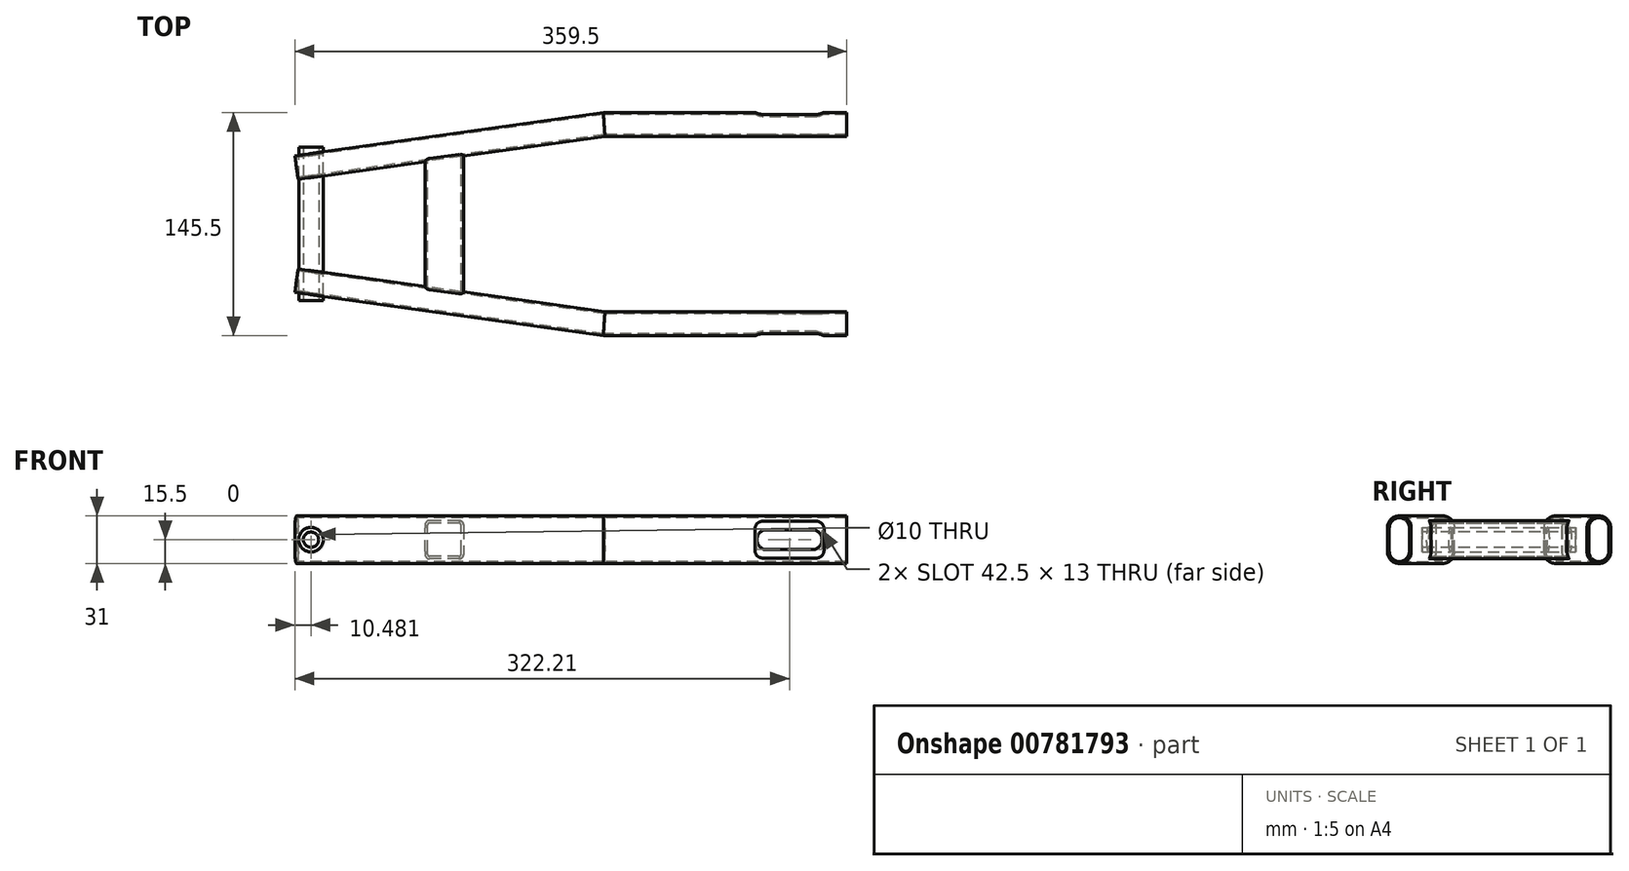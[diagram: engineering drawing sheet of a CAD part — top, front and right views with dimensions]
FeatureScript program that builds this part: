
annotation { "Feature Type Name" : "Feature", "Feature Type Description" : "" }
export const myFeature = defineFeature(function(context is Context, id is Id, definition is map)
    precondition{}
    {
        {
            var Q0;
            Q0=qCreatedBy(makeId("Top.planeOp"),FACE);
            var sketch = newSketch(context, id + "F0", { "sketchPlane" : qUnion([Q0])});
            skLineSegment(sketch, "E0", {"start": v(0, 65) * mm, "end": v(-158.03, 65) * mm});
            skLineSegment(sketch, "E1", {"start": v(-158.03, 65) * mm, "end": v(-358.42, 36.84) * mm});
            skSolve(sketch);
        }
        {
            var Q0;
            Q0=qCreatedBy(makeId("Right.planeOp"),FACE);
            var sketch = newSketch(context, id + "F1", { "sketchPlane" : qUnion([Q0])});
            skLineSegment(sketch, "E2.left", {"start": v(72.75, -7.75) * mm, "end": v(72.75, 7.75) * mm});
            skLineSegment(sketch, "E2.right", {"start": v(57.25, -7.75) * mm, "end": v(57.25, 7.75) * mm});
            skArc(sketch, "E3", {"start": v(57.25, 7.75) * mm, "mid": v(65, 15.5) * mm, "end": v(72.75, 7.75) * mm});
            skArc(sketch, "E4", {"start": v(72.75, -7.75) * mm, "mid": v(65, -15.5) * mm, "end": v(57.25, -7.75) * mm});
            skLineSegment(sketch, "E5.0", {"start": v(58.45, -7.75) * mm, "end": v(58.45, 7.75) * mm});
            skLineSegment(sketch, "E6.0", {"start": v(71.55, -7.75) * mm, "end": v(71.55, 7.75) * mm});
            skArc(sketch, "E7.0", {"start": v(71.55, -7.75) * mm, "mid": v(65, -14.3) * mm, "end": v(58.45, -7.75) * mm});
            skArc(sketch, "E8.0", {"start": v(58.45, 7.75) * mm, "mid": v(65, 14.3) * mm, "end": v(71.55, 7.75) * mm});
            skSolve(sketch);
        }
        {
            var Q0;
            Q0 = qSketchRegion(id + "F1", true);
            var Q1;
            Q1 = qConstructionFilter(qBodyType(qCreatedBy(id + "F0" ,EDGE), BodyType.WIRE), ConstructionObject.NO);
            sweep(context, id + "F2", {"profiles" : qUnion([Q0]), "path" : qUnion([Q1])});
        }
        {
            var Q0;
            Q0=makeQuery(id+"F2.opSweep","SWEPT_FACE",FACE,{"disambiguationData":[OSD([sQuery(id+"F0.wireOp",EDGE,"E0"),sQuery(id+"F1.wireOp",EDGE,"E2.right")])]});
            var sketch = newSketch(context, id + "F3", { "sketchPlane" : qUnion([Q0])});
            skLineSegment(sketch, "E9.bottom", {"start": v(-22.54, -6.5) * mm, "end": v(-52.04, -6.5) * mm});
            skLineSegment(sketch, "E9.top", {"start": v(-22.54, 6.5) * mm, "end": v(-52.04, 6.5) * mm});
            skPoint(sketch, "E9.middle", {"position": v(-37.3, 0) * mm});
            skArc(sketch, "E10", {"start": v(-22.54, 6.5) * mm, "mid": v(-16.04, 0) * mm, "end": v(-22.54, -6.5) * mm});
            skArc(sketch, "E11", {"start": v(-52.04, 6.5) * mm, "mid": v(-58.54, 0) * mm, "end": v(-52.04, -6.5) * mm});
            skSolve(sketch);
        }
        {
            var Q0;
            Q0=makeQuery(id+"F3.imprint","IMPRINT",FACE,{"disambiguationData":[TD([[makeQuery(id+"F3.imprint","IMPRINT",EDGE,{"derivedFrom":sQuery(id+"F3.wireOp",EDGE,"E9.bottom")}),-1.0]])]});
            extrude(context, id + "F4", {"entities" : qUnion([Q0]), "operationType" : NewBodyOperationType.REMOVE, "oppositeDirection" : true, "depth" : 5 * mm, "offsetDistance" : 25 * mm});
        }
        {
            var Q0;
            Q0=makeQuery(id+"F2.opSweep","SWEPT_FACE",FACE,{"disambiguationData":[OSD([sQuery(id+"F0.wireOp",EDGE,"E0"),sQuery(id+"F1.wireOp",EDGE,"E2.left")])]});
            var sketch = newSketch(context, id + "F5", { "sketchPlane" : qUnion([Q0])});
            skLineSegment(sketch, "E12.bottom", {"start": v(54.76, -12) * mm, "end": v(19.76, -12) * mm});
            skLineSegment(sketch, "E12.top", {"start": v(54.76, 12) * mm, "end": v(19.76, 12) * mm});
            skLineSegment(sketch, "E12.left", {"start": v(59.76, -7) * mm, "end": v(59.76, 7) * mm});
            skLineSegment(sketch, "E12.right", {"start": v(14.76, -7) * mm, "end": v(14.76, 7) * mm});
            skPoint(sketch, "E12.middle", {"position": v(37.26, 0) * mm});
            skPoint(sketch, "E13.visualSharp", {"position": v(59.76, 12) * mm});
            skArc(sketch, "E13.filletArc", {"start": v(59.76, 7) * mm, "mid": v(58.3, 10.54) * mm, "end": v(54.76, 12) * mm});
            skPoint(sketch, "E14.visualSharp", {"position": v(59.76, -12) * mm});
            skArc(sketch, "E14.filletArc", {"start": v(54.76, -12) * mm, "mid": v(58.3, -10.54) * mm, "end": v(59.76, -7) * mm});
            skPoint(sketch, "E15.visualSharp", {"position": v(14.76, -12) * mm});
            skArc(sketch, "E15.filletArc", {"start": v(14.76, -7) * mm, "mid": v(16.22, -10.54) * mm, "end": v(19.76, -12) * mm});
            skPoint(sketch, "E16.visualSharp", {"position": v(14.76, 12) * mm});
            skArc(sketch, "E16.filletArc", {"start": v(19.76, 12) * mm, "mid": v(16.22, 10.54) * mm, "end": v(14.76, 7) * mm});
            skSolve(sketch);
        }
        {
            var Q0;
            Q0 = qSketchRegion(id + "F5", true);
            extrude(context, id + "F6", {"entities" : qUnion([Q0]), "operationType" : NewBodyOperationType.REMOVE, "oppositeDirection" : true, "depth" : 3 * mm, "offsetDistance" : 25 * mm});
        }
        {
            var Q0;
            Q0=makeQuery(id+"F2.opSweep","SWEPT_BODY",BODY,{"disambiguationData":[OSD([sQuery(id+"F0.wireOp",EDGE,"E1"),sQuery(id+"F1.wireOp",EDGE,"E2.left"),sQuery(id+"F1.wireOp",EDGE,"E2.right"),sQuery(id+"F1.wireOp",EDGE,"E3"),sQuery(id+"F1.wireOp",EDGE,"E4"),sQuery(id+"F1.wireOp",EDGE,"E5.0"),sQuery(id+"F1.wireOp",EDGE,"E6.0"),sQuery(id+"F1.wireOp",EDGE,"E7.0"),sQuery(id+"F1.wireOp",EDGE,"E8.0")])]});
            var Q1;
            Q1=qCreatedBy(makeId("Front.planeOp"),FACE);
            mirror(context, id + "F7", {"entities" : qUnion([Q0]), "mirrorPlane" : qUnion([Q1])});
        }
        {
            var Q0;
            Q0=qCreatedBy(makeId("Front.planeOp"),FACE);
            var sketch = newSketch(context, id + "F8", { "sketchPlane" : qUnion([Q0])});
            skLineSegment(sketch, "E17.bottom", {"start": v(-252.69, 12.5) * mm, "end": v(-271.69, 12.5) * mm});
            skLineSegment(sketch, "E17.top", {"start": v(-252.69, -12.5) * mm, "end": v(-271.69, -12.5) * mm});
            skLineSegment(sketch, "E17.left", {"start": v(-249.69, 9.5) * mm, "end": v(-249.69, -9.5) * mm});
            skLineSegment(sketch, "E17.right", {"start": v(-274.69, 9.5) * mm, "end": v(-274.69, -9.5) * mm});
            skPoint(sketch, "E17.middle", {"position": v(-262.19, 0) * mm});
            skLineSegment(sketch, "E18.0", {"start": v(-252.69, 10.9) * mm, "end": v(-271.69, 10.9) * mm});
            skLineSegment(sketch, "E19.0", {"start": v(-251.29, 9.5) * mm, "end": v(-251.29, -9.5) * mm});
            skLineSegment(sketch, "E20.0", {"start": v(-252.69, -10.9) * mm, "end": v(-271.69, -10.9) * mm});
            skLineSegment(sketch, "E21.0", {"start": v(-273.09, 9.5) * mm, "end": v(-273.09, -9.5) * mm});
            skPoint(sketch, "E22.visualSharp", {"position": v(-249.69, 12.5) * mm});
            skArc(sketch, "E22.filletArc", {"start": v(-249.69, 9.5) * mm, "mid": v(-250.57, 11.62) * mm, "end": v(-252.69, 12.5) * mm});
            skPoint(sketch, "E23.visualSharp", {"position": v(-274.69, 12.5) * mm});
            skArc(sketch, "E23.filletArc", {"start": v(-271.69, 12.5) * mm, "mid": v(-273.81, 11.62) * mm, "end": v(-274.69, 9.5) * mm});
            skPoint(sketch, "E24.visualSharp", {"position": v(-274.69, -12.5) * mm});
            skArc(sketch, "E24.filletArc", {"start": v(-274.69, -9.5) * mm, "mid": v(-273.81, -11.62) * mm, "end": v(-271.69, -12.5) * mm});
            skPoint(sketch, "E25.visualSharp", {"position": v(-249.69, -12.5) * mm});
            skArc(sketch, "E25.filletArc", {"start": v(-252.69, -12.5) * mm, "mid": v(-250.57, -11.62) * mm, "end": v(-249.69, -9.5) * mm});
            skPoint(sketch, "E26.visualSharp", {"position": v(-251.29, -10.9) * mm});
            skArc(sketch, "E26.filletArc", {"start": v(-252.69, -10.9) * mm, "mid": v(-251.7, -10.49) * mm, "end": v(-251.29, -9.5) * mm});
            skPoint(sketch, "E27.visualSharp", {"position": v(-251.29, 10.9) * mm});
            skArc(sketch, "E27.filletArc", {"start": v(-251.29, 9.5) * mm, "mid": v(-251.7, 10.49) * mm, "end": v(-252.69, 10.9) * mm});
            skPoint(sketch, "E28.visualSharp", {"position": v(-273.09, 10.9) * mm});
            skArc(sketch, "E28.filletArc", {"start": v(-271.69, 10.9) * mm, "mid": v(-272.68, 10.49) * mm, "end": v(-273.09, 9.5) * mm});
            skPoint(sketch, "E29.visualSharp", {"position": v(-273.09, -10.9) * mm});
            skArc(sketch, "E29.filletArc", {"start": v(-273.09, -9.5) * mm, "mid": v(-272.68, -10.49) * mm, "end": v(-271.69, -10.9) * mm});
            skSolve(sketch);
        }
        {
            var Q0;
            Q0 = qSketchRegion(id + "F8", true);
            extrude(context, id + "F9", {"entities" : qUnion([Q0]), "operationType" : NewBodyOperationType.ADD, "endBound" : BoundingType.UP_TO_NEXT, "depth" : 25 * mm, "offsetDistance" : 25 * mm, "hasSecondDirection" : true, "secondDirectionBound" : SecondDirectionBoundingType.UP_TO_NEXT, "secondDirectionOppositeDirection" : true, "secondDirectionDepth" : 25 * mm});
        }
        {
            var Q0;
            Q0=qCreatedBy(makeId("Front.planeOp"),FACE);
            var sketch = newSketch(context, id + "F10", { "sketchPlane" : qUnion([Q0])});
            skCircle(sketch, "E30", {"center": v(-349.02, 0) * mm, "radius": 8 * mm});
            skSolve(sketch);
        }
        {
            var Q0;
            Q0 = qSketchRegion(id + "F10", true);
            extrude(context, id + "F11", {"entities" : qUnion([Q0]), "operationType" : NewBodyOperationType.ADD, "endBound" : BoundingType.SYMMETRIC, "depth" : 100 * mm, "offsetDistance" : 25 * mm});
        }
        {
            var Q0;
            Q0=makeQuery(id+"F11.opExtrude","CAP_FACE",FACE,{"disambiguationData":[OSD([sQuery(id+"F10.wireOp",EDGE,"E30")])],"isStart":false});
            var sketch = newSketch(context, id + "F12", { "sketchPlane" : qUnion([Q0])});
            skCircle(sketch, "E31", {"center": v(-349.02, 0) * mm, "radius": 5 * mm});
            skSolve(sketch);
        }
        {
            var Q0;
            Q0 = qSketchRegion(id + "F12", true);
            extrude(context, id + "F13", {"entities" : qUnion([Q0]), "operationType" : NewBodyOperationType.REMOVE, "endBound" : BoundingType.THROUGH_ALL, "oppositeDirection" : true, "depth" : 25 * mm, "offsetDistance" : 25 * mm});
        }
    });
